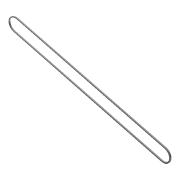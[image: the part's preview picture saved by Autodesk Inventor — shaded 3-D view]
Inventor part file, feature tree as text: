
AUTODESK INVENTOR PART (.ipt)
format: ipt  version: 2012 (Build 160160000, 160)  size: 88,576 bytes
history: native  units: in
note: dims shown in document units (in); Inventor stores cm internally (conversion verified against a paired STEP export)
features: extrude x1, fillet x1, sketch x1
ambient origin geometry x8: Origin, YZ Plane, XZ Plane, XY Plane, X Axis, Y Axis, Z Axis, Center Point
bodies: Solid1 (feature_tree)
feature tree (3):
  extrude  "Extrusion1"  Depth=0.1875in
  fillet  "Fillet1"  Radius=0.1875in
  sketch  "Sketch1"  dims[d0=1.0in d1=0.1875in d2=0.1875in d3=0.0in d4=0.0938in]
